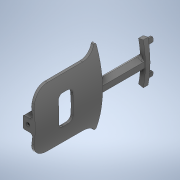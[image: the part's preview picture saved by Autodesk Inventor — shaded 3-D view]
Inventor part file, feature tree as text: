
AUTODESK INVENTOR PART (.ipt)
format: ipt  version: 2021 (Build 250183000, 183)  size: 710,656 bytes
history: native  units: mm
features: projected_geometry x39, extrude x19, sketch x18, fillet x12, plane x1
ambient origin geometry x8: Origin, YZ Plane, XZ Plane, XY Plane, X Axis, Y Axis, Z Axis, Center Point
bodies: Solid1 (feature_tree)
feature tree (89):
  extrude  "Extrusion1"  Depth=88.0mm
  fillet  "Fillet1"  Radius=5.61996mm
  extrude  "Extrusion2"  Depth=2.80998mm
  fillet  "Fillet2"  Radius=5.61996mm
  fillet  "Fillet3"  Radius=90.0mm
  extrude  "Extrusion3"  Depth=84.0mm
  fillet  "Fillet4"  Radius=29.670597mm
  plane  "Work Plane1"
  extrude  "Extrusion4"  Depth=29.670597mm
  extrude  "Extrusion5"  Depth=7.95mm TaperAngle=0.0deg
  extrude  "Extrusion6"  Depth=4.0mm
  fillet  "Fillet5"  Radius=2.0mm
  extrude  "Extrusion7"  Depth=2.443461mm
  extrude  "Extrusion8"  Depth=1.0mm
  extrude  "Extrusion9"  TaperAngle=0.0deg  [1 undecoded]
  extrude  "Extrusion10"  Depth=8.2mm
  sketch  "Sketch12"  dims[d34=46.4mm d35=0.0mm d36=1.6mm d37=0.0mm d38=2.0mm]
  extrude  "Extrusion11"  Depth=1.6mm TaperAngle=0.0deg
  fillet  "Fillet9"  Radius=2.0mm
  extrude  "Extrusion12"  Depth=8.0mm TaperAngle=0.0deg
  extrude  "Extrusion13"  Depth=26.87807mm
  extrude  "Extrusion14"  Depth=88.0mm
  fillet  "Fillet10"  Radius=88.0mm
  extrude  "Extrusion15"  Depth=88.0mm
  extrude  "Extrusion16"  Depth=15.0mm TaperAngle=0.0deg
  fillet  "Fillet11"  Radius=81.45mm
  fillet  "Fillet12"  Radius=15.0mm
  fillet  "Fillet13"  Radius=29.452431mm
  extrude  "Extrusion17"  Depth=0.9mm TaperAngle=0.0deg
  fillet  "Fillet14"  Radius=28.0mm
  extrude  "Extrusion18"  Depth=10.0mm
  extrude  "Extrusion19"  Depth=10.0mm
  fillet  "Fillet15"  Radius=38.65mm
  sketch  "Sketch1"  dims[d0=88.0mm d1=2.80998mm d2=5.61996mm]
  sketch  "Sketch2"  dims[d3=86.0mm d4=2.80998mm d5=5.61996mm d6=90.0mm d7=0.0mm]
  projected_geometry  "Projected Loop1"
  sketch  "Sketch3"  dims[d8=14.0mm d9=84.0mm d10=29.670597mm]
  projected_geometry  "Projected Loop2"
  sketch  "Sketch5"  dims[d11=3.490659mm d12=29.670597mm]
  projected_geometry  "Projected Loop4"
  projected_geometry  "Projected Loop5"
  projected_geometry  "Projected Loop6"
  projected_geometry  "Projected Loop7"
  sketch  "Sketch6"  dims[d13=29.670597mm d14=7.95mm d15=16.0mm d16=0.0mm d17=0.0mm]
  projected_geometry  "Projected Loop8"
  sketch  "Sketch7"  dims[d18=14.0mm d19=4.0mm d20=2.0mm]
  projected_geometry  "Projected Loop9"
  projected_geometry  "Projected Loop10"
  projected_geometry  "Projected Loop11"
  projected_geometry  "Projected Loop12"
  projected_geometry  "Projected Loop13"
  projected_geometry  "Projected Loop14"
  projected_geometry  "Projected Loop15"
  projected_geometry  "Projected Loop16"
  projected_geometry  "Projected Loop17"
  sketch  "Sketch8"  dims[d21=30.194196mm d22=2.443461mm]
  projected_geometry  "Projected Loop18"
  sketch  "Sketch9"  dims[d23=4.2mm d24=0.0mm d25=1.0mm]
  projected_geometry  "Projected Loop19"
  projected_geometry  "Projected Loop20"
  projected_geometry  "Projected Loop21"
  sketch  "Sketch10"  dims[d29=10.0mm d30=0.0mm d31=0.0mm]
  projected_geometry  "Projected Loop22"
  sketch  "Sketch11"  dims[d32=83.5mm d33=8.2mm]
  projected_geometry  "Projected Loop23"
  projected_geometry  "Projected Loop24"
  projected_geometry  "Projected Loop25"
  projected_geometry  "Projected Loop26"
  sketch  "Sketch13"  dims[d39=6.0mm d40=0.0mm d43=8.0mm d44=0.0mm]
  projected_geometry  "Projected Loop27"
  sketch  "Sketch14"  dims[d45=86.0mm d46=26.87807mm]
  sketch  "Sketch15"  dims[d47=86.0mm d48=26.87807mm d49=88.0mm]
  projected_geometry  "Projected Loop28"
  sketch  "Sketch16"  dims[d50=26.87807mm d51=88.0mm]
  sketch  "Sketch17"  dims[d52=26.87807mm d53=15.0mm d54=0.0mm d56=81.45mm d57=15.0mm d58=0.0mm d59=29.452431mm]
  projected_geometry  "Projected Loop29"
  projected_geometry  "Projected Loop30"
  projected_geometry  "Projected Loop31"
  projected_geometry  "Projected Loop32"
  projected_geometry  "Projected Loop33"
  projected_geometry  "Projected Loop34"
  projected_geometry  "Projected Loop35"
  projected_geometry  "Projected Loop36"
  projected_geometry  "Projected Loop37"
  sketch  "Sketch18"  dims[d60=29.452431mm d61=0.9mm d62=0.0mm d63=28.0mm]
  sketch  "Sketch19"  dims[d64=28.0mm d65=13.2mm d66=13.2mm d67=38.65mm d68=38.65mm d69=27.85mm d70=27.85mm d71=29.0mm d72=29.0mm d73=28.0mm d74=28.0mm d75=100.0mm d76=0.0mm d77=0.0mm d78=1.0mm d79=3.0mm d80=0.0mm d81=3.0mm d82=0.0mm d83=86.917mm d84=0.0mm d85=3.0mm d86=0.0mm d87=82.0mm d88=8.0mm d89=10.0mm d90=10.0mm d91=0.0mm d92=2.0mm d93=2.6mm d94=5.6mm d95=2.8mm d96=1.3mm d97=5.6mm d98=0.0mm d99=60.0deg d100=60.0deg d101=6.0mm d102=0.0mm d103=2.0mm d104=1.0mm d105=2.0mm d106=12.0mm d107=22.0mm d108=24.0mm d109=2.755305mm d110=12.0mm d111=4.0mm d112=85.8mm d113=29.757864mm d114=3.316126mm d115=84.2mm d116=3.316126mm d117=10.0mm d118=0.0mm d119=0.5mm d120=5.2mm d121=1.9mm d122=0.0mm d123=0.2mm d124=0.0mm d125=10.0mm d126=0.872665mm]
  projected_geometry  "Projected Loop38"
  projected_geometry  "Projected Loop39"
  projected_geometry  "Projected Loop40"
note: 1 required parameter value undecoded (feature->parameter linkage not recoverable at this tier; creation-order binding heuristic only, values carry confidence <= 0.55)
